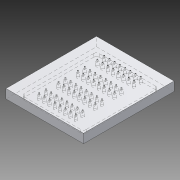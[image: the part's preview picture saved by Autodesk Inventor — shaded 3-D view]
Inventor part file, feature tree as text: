
AUTODESK INVENTOR PART (.ipt)
format: ipt  version: 2013 (Build 170138000, 138)  size: 293,376 bytes
history: native  units: mm
features: sketch x3, extrude x2, hole x1, pattern_linear x1, fillet x1, reference x1
ambient origin geometry x8: Origin, YZ Plane, XZ Plane, XY Plane, X Axis, Y Axis, Z Axis, Center Point
bodies: Volumenkörper1 (feature_tree)
feature tree (9):
  extrude  "Extrusion1"  Depth=140.0mm
  hole  "Bohrung1"  [1 undecoded]
  pattern_linear  "Rechteckige Anordnung1"  Spacing1=5.3mm  [1 undecoded]
  extrude  "Extrusion2"  Depth=5.3mm
  fillet  "Rundung1"  Radius=10.56mm
  sketch  "Skizze1"  dims[d0=120.0mm d3=140.0mm]
  sketch  "Skizze2"  dims[d4=14.0mm d5=0.0mm d6=4.05mm]
  reference  "Referenz1"
  sketch  "Skizze3"  dims[d7=4.05mm d8=5.3mm d9=5.3mm d10=10.56mm d11=80.0mm d13=8.1mm d14=10.0mm d16=10.0mm d18=1.5mm d19=6.0mm d20=4.0mm d21=11.0mm d22=90.0deg d23=8.0mm d24=20.594885mm d25=40.0mm d27=30.0mm d28=12.0mm d29=5.0mm d30=0.0mm d31=4.0mm]
note: 2 required parameter values undecoded (feature->parameter linkage not recoverable at this tier; creation-order binding heuristic only, values carry confidence <= 0.55)
